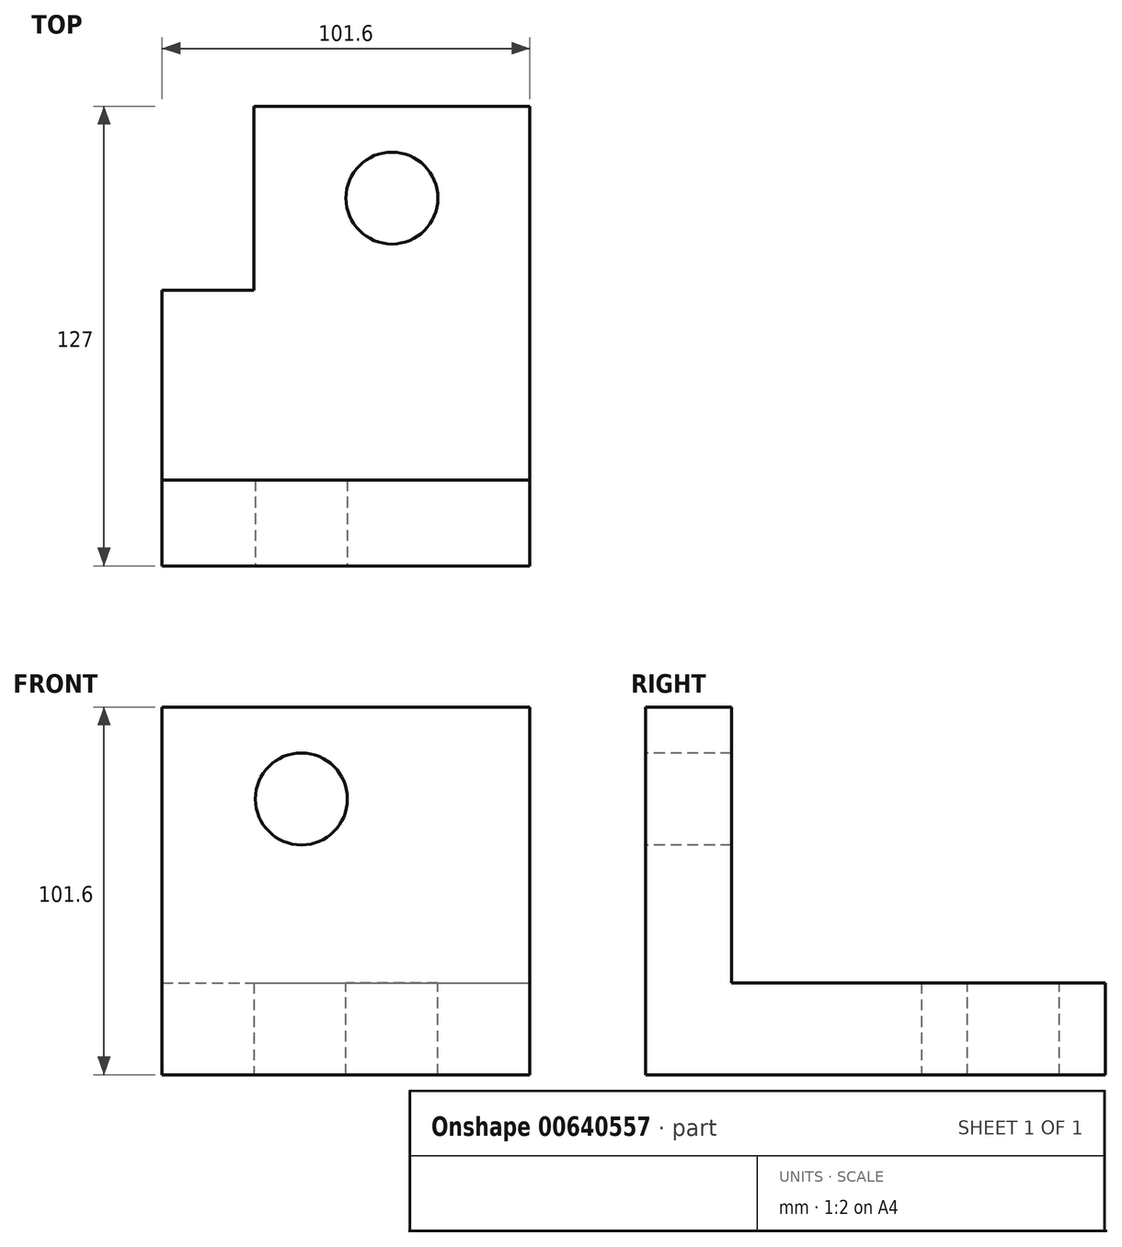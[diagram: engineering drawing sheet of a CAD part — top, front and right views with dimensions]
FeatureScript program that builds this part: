
annotation { "Feature Type Name" : "Feature", "Feature Type Description" : "" }
export const myFeature = defineFeature(function(context is Context, id is Id, definition is map)
    precondition{}
    {
        {
            var Q0;
            Q0=qCreatedBy(makeId("Top.planeOp"),FACE);
            var sketch = newSketch(context, id + "F0", { "sketchPlane" : qUnion([Q0])});
            skLineSegment(sketch, "E0.bottom", {"start": v(-13.1, 63.98) * mm, "end": v(63.1, 63.98) * mm});
            skLineSegment(sketch, "E0.top", {"start": v(38.08, -139.22) * mm, "end": v(63.1, -139.22) * mm});
            skLineSegment(sketch, "E0.left", {"start": v(-38.5, 13.18) * mm, "end": v(-38.5, -63.02) * mm});
            skLineSegment(sketch, "E0.right", {"start": v(63.1, 63.98) * mm, "end": v(63.1, -139.22) * mm});
            skLineSegment(sketch, "E1", {"start": v(-38.5, 13.18) * mm, "end": v(-13.1, 13.18) * mm});
            skLineSegment(sketch, "E2", {"start": v(-13.1, 13.18) * mm, "end": v(-13.1, 63.98) * mm});
            skPoint(sketch, "E3.orphan", {"position": v(-38.5, 63.98) * mm});
            skLineSegment(sketch, "E4", {"start": v(-38.5, -63.02) * mm, "end": v(38.08, -63.02) * mm});
            skLineSegment(sketch, "E5", {"start": v(38.08, -63.02) * mm, "end": v(38.08, -139.22) * mm});
            skLineSegment(sketch, "E6", {"start": v(-38.5, 13.18) * mm, "end": v(-38.5, -39.32) * mm});
            skLineSegment(sketch, "E7", {"start": v(-38.5, -39.32) * mm, "end": v(63.1, -39.32) * mm});
            skLineSegment(sketch, "E8", {"start": v(63.1, -39.32) * mm, "end": v(63.1, -139.22) * mm});
            skPoint(sketch, "E9.orphan", {"position": v(-38.5, -139.22) * mm});
            skLineSegment(sketch, "E10", {"start": v(38.08, -63.02) * mm, "end": v(63.1, -63.02) * mm});
            skSolve(sketch);
        }
        {
            var Q0;
            Q0=makeQuery(id+"F0.imprint","IMPRINT",FACE,{"disambiguationData":[TD([[makeQuery(id+"F0.imprint","IMPRINT",EDGE,{"derivedFrom":sQuery(id+"F0.wireOp",EDGE,"E0.left")}),1.0]])]});
            extrude(context, id + "F1", {"entities" : qUnion([Q0]), "depth" : 101.6 * mm, "offsetDistance" : 25.4 * mm});
        }
        {
            var Q0;
            Q0=makeQuery(id+"F0.imprint","IMPRINT",FACE,{"disambiguationData":[TD([[makeQuery(id+"F0.imprint","IMPRINT",EDGE,{"derivedFrom":sQuery(id+"F0.wireOp",EDGE,"E0.bottom")}),-1.0]])]});
            extrude(context, id + "F2", {"entities" : qUnion([Q0]), "operationType" : NewBodyOperationType.ADD, "depth" : 25.4 * mm, "offsetDistance" : 25.4 * mm});
        }
        {
            var Q0;
            Q0=makeQuery(id+"F1.opExtrude","SWEPT_FACE",FACE,{"disambiguationData":[OSD([sQuery(id+"F0.wireOp",EDGE,"E4")])]});
            var sketch = newSketch(context, id + "F3", { "sketchPlane" : qUnion([Q0])});
            skLineSegment(sketch, "E11", {"start": v(0, 101.6) * mm, "end": v(0, 88.9) * mm, "construction": true});
            skLineSegment(sketch, "E12", {"start": v(0, 88.9) * mm, "end": v(0, 76.2) * mm, "construction": true});
            skCircle(sketch, "E13", {"center": v(0, 76.2) * mm, "radius": 12.7 * mm});
            skSolve(sketch);
        }
        {
            var Q0;
            Q0=makeQuery(id+"F3.imprint","IMPRINT",FACE,{"disambiguationData":[TD([[makeQuery(id+"F3.imprint","IMPRINT",EDGE,{"derivedFrom":sQuery(id+"F3.wireOp",EDGE,"E13")}),1.0]])]});
            extrude(context, id + "F4", {"entities" : qUnion([Q0]), "operationType" : NewBodyOperationType.REMOVE, "endBound" : BoundingType.THROUGH_ALL, "oppositeDirection" : true, "depth" : 25.4 * mm, "offsetDistance" : 25.4 * mm});
        }
        {
            var Q0;
            Q0=makeQuery(id+"F2.opExtrude","CAP_FACE",FACE,{"disambiguationData":[OSD([sQuery(id+"F0.wireOp",EDGE,"E0.bottom"),sQuery(id+"F0.wireOp",EDGE,"E0.right"),sQuery(id+"F0.wireOp",EDGE,"E1"),sQuery(id+"F0.wireOp",EDGE,"E2"),sQuery(id+"F0.wireOp",EDGE,"E6"),sQuery(id+"F0.wireOp",EDGE,"E7")])],"isStart":false});
            var sketch = newSketch(context, id + "F5", { "sketchPlane" : qUnion([Q0])});
            skLineSegment(sketch, "E14", {"start": v(25, 63.98) * mm, "end": v(25, 38.58) * mm, "construction": true});
            skCircle(sketch, "E15", {"center": v(25, 38.58) * mm, "radius": 12.7 * mm});
            skSolve(sketch);
        }
        {
            var Q0;
            Q0=makeQuery(id+"F5.imprint","IMPRINT",FACE,{"disambiguationData":[TD([[makeQuery(id+"F5.imprint","IMPRINT",EDGE,{"derivedFrom":sQuery(id+"F5.wireOp",EDGE,"E15")}),1.0]])]});
            extrude(context, id + "F6", {"entities" : qUnion([Q0]), "operationType" : NewBodyOperationType.REMOVE, "endBound" : BoundingType.THROUGH_ALL, "oppositeDirection" : true, "depth" : 25.4 * mm, "offsetDistance" : 25.4 * mm});
        }
    });
